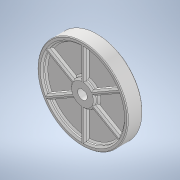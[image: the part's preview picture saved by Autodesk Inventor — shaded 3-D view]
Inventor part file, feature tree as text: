
AUTODESK INVENTOR PART (.ipt)
format: ipt  version: 2020.2 (Build 242310000, 310)  size: 402,944 bytes
history: native  units: mm
features: extrude x2, chamfer x2, sketch x2, fillet x1, mirror x1
ambient origin geometry x8: Origin, YZ Plane, XZ Plane, XY Plane, X Axis, Y Axis, Z Axis, Center Point
bodies: Solid1 (feature_tree)
feature tree (8):
  extrude  "Extrusion1"  Depth=0.2mm
  extrude  "Extrusion2"  Depth=0.5mm
  chamfer  "Chamfer1"  Distance=3.0mm
  chamfer  "Chamfer2"  Distance=3.0mm
  fillet  "Fillet1"  Radius=1.5mm
  mirror  "Mirror2"
  sketch  "Sketch1"  dims[d0=60.0mm d1=0.2mm]
  sketch  "Sketch2"  dims[d2=5.0mm d3=0.0mm d4=5.0mm d5=3.0mm d6=3.0mm d7=1.5mm d8=0.0mm d9=60.0mm d11=360.0deg d13=3.0mm d14=0.0mm d15=1.0mm d16=2.0mm d17=45.0deg d18=1.0mm d19=2.0mm d20=45.0deg d21=0.5mm]
